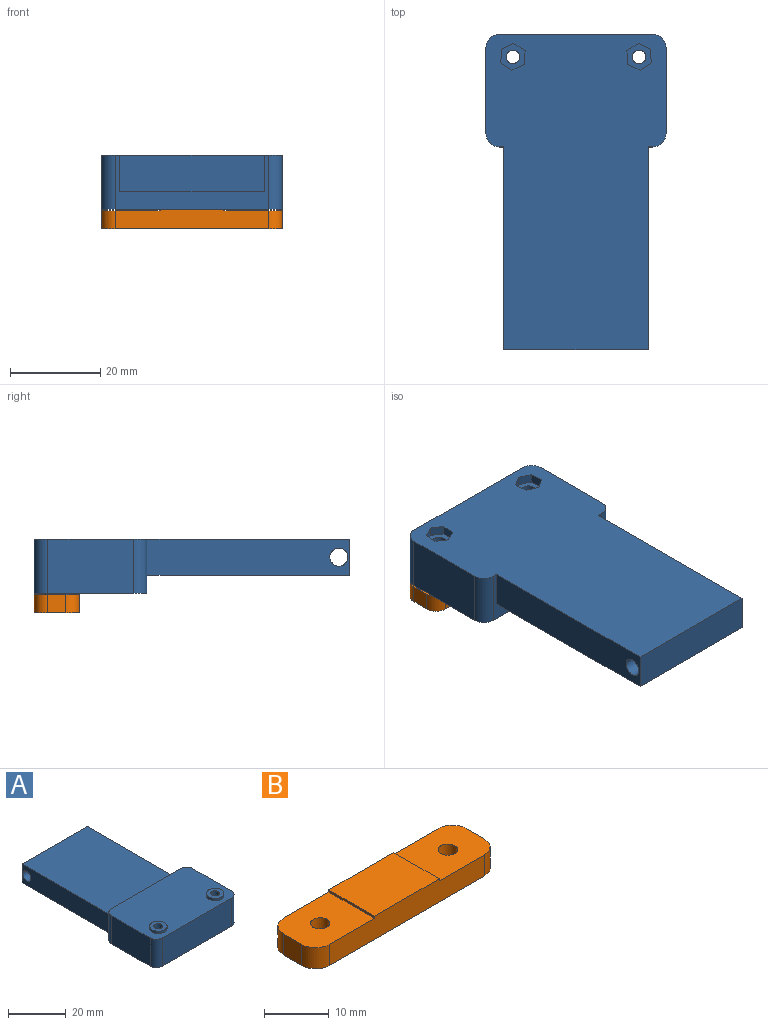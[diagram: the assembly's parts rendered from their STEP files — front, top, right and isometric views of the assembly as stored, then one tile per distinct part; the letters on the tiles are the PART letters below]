
ASSEMBLY  parts=2 mates=1
PART A: 35 faces, bbox 40x70x13 mm
  f0: plane 70x40mm, normal (0,0,-1), area 2385.4mm2, adj f2,f3,f4,f6,f8,f9,f10,f16
  f1: plane 40x25mm, normal (0,0,1), area 933.8mm2, adj f2,f3,f4,f6,f12,f14,f16,f17
  f2: plane 19x12mm, normal (-1,0,0), area 228mm2, adj f0,f1,f16,f18
  f3: plane 34x12mm, normal (0,-1,0), area 408mm2, adj f0,f1,f16,f17
  f4: plane 19x12mm, normal (1,0,0), area 228mm2, adj f0,f1,f17,f19
  f5: cylinder r=1.5mm len=11mm, axis (0,0,-1), area 103.7mm2, adj f15,f34
  f6: plane 34x12mm, normal (0,1,0), area 152mm2, adj f0,f1,f8,f9,f11,f18,f19
  f7: cylinder r=1.5mm len=11mm, axis (0,0,-1), area 103.7mm2, adj f13,f27
  f8: plane 45x8mm, normal (-1,0,0), area 347.4mm2, adj f0,f6,f10,f11,f20
  f9: plane 45x8mm, normal (1,0,0), area 347.4mm2, adj f0,f6,f10,f11,f20
  f10: plane 32x8mm, normal (0,1,0), area 256mm2, adj f0,f8,f9,f11
  f11: plane 45x32mm, normal (0,0,1), area 1440mm2, adj f6,f8,f9,f10
  f12: cylinder r=3.05mm len=6.1mm, axis (0,0,-1), area 19.2mm2, adj f1,f13
  f13: plane 6.1x6.1mm, normal (0,0,1), area 22.2mm2, adj f7,f12
  f14: cylinder r=3.05mm len=6.1mm, axis (0,0,-1), area 19.2mm2, adj f1,f15
  f15: plane 6.1x6.1mm, normal (0,0,1), area 22.2mm2, adj f5,f14
  f16: cylinder r=3mm len=12mm, axis (0,0,-1), area 56.5mm2, adj f0,f1,f2,f3
  f17: cylinder r=3mm len=12mm, axis (0,0,1), area 56.5mm2, adj f0,f1,f3,f4
  f18: cylinder r=3mm len=12mm, axis (0,0,1), area 56.5mm2, adj f0,f1,f2,f6
  f19: cylinder r=3mm len=12mm, axis (0,0,-1), area 56.5mm2, adj f0,f1,f4,f6
  f20: cylinder r=2mm len=32mm, axis (-1,0,0), area 402.1mm2, adj f8,f9
  f21: plane 2.99x2mm, normal (-1,-0.07,0), area 6mm2, adj f0,f22,f26,f27
  f22: plane 2.7x2mm, normal (-0.44,-0.9,0), area 6mm2, adj f0,f21,f23,f27
  f23: plane 2.49x2mm, normal (0.56,-0.83,0), area 6mm2, adj f0,f22,f24,f27
  f24: plane 2.99x2mm, normal (1,0.07,0), area 6mm2, adj f0,f23,f25,f27
  f25: plane 2.7x2mm, normal (0.44,0.9,0), area 6mm2, adj f0,f24,f26,f27
  f26: plane 2.49x2mm, normal (-0.56,0.83,0), area 6mm2, adj f0,f21,f25,f27
  f27: plane 5.99x5.4mm, normal (0,0,-1), area 16.3mm2, adj f7,f21,f22,f23,f24,f25,f26
  f28: plane 2.7x2mm, normal (0.44,-0.9,0), area 6mm2, adj f0,f29,f33,f34
  f29: plane 2.99x2mm, normal (1,-0.07,0), area 6mm2, adj f0,f28,f30,f34
  f30: plane 2.49x2mm, normal (0.56,0.83,0), area 6mm2, adj f0,f29,f31,f34
  f31: plane 2.7x2mm, normal (-0.44,0.9,0), area 6mm2, adj f0,f30,f32,f34
  f32: plane 2.99x2mm, normal (-1,0.07,0), area 6mm2, adj f0,f31,f33,f34
  f33: plane 2.49x2mm, normal (-0.56,-0.83,0), area 6mm2, adj f0,f28,f32,f34
  f34: plane 5.99x5.4mm, normal (0,0,-1), area 16.3mm2, adj f5,f28,f29,f30,f31,f32,f33
PART B: 16 faces, bbox 40x10x4.4 mm
  f0: plane 12.9x10mm, normal (0,0,1), area 118.1mm2, adj f2,f3,f4,f5,f10,f14,f15
  f1: plane 4x4mm, normal (-1,0,0), area 16mm2, adj f7,f8,f12,f13
  f2: plane 34x4.4mm, normal (0,-1,0), area 141.7mm2, adj f0,f7,f8,f9,f10,f11,f12,f14
  f3: plane 4x4mm, normal (1,0,0), area 16mm2, adj f0,f8,f14,f15
  f4: cylinder r=1.5mm len=4mm, axis (0,0,-1), area 37.7mm2, adj f0,f8
  f5: plane 34x4.4mm, normal (0,1,0), area 141.7mm2, adj f0,f7,f8,f9,f10,f11,f13,f15
  f6: cylinder r=1.5mm len=4mm, axis (0,0,-1), area 37.7mm2, adj f7,f8
  f7: plane 12.9x10mm, normal (0,0,1), area 118.1mm2, adj f1,f2,f5,f6,f9,f12,f13
  f8: plane 40x10mm, normal (0,0,-1), area 378.1mm2, adj f1,f2,f3,f4,f5,f6,f12,f13
  f9: plane 10x0.4mm, normal (-1,0,0), area 4mm2, adj f2,f5,f7,f11
  f10: plane 10x0.4mm, normal (1,0,0), area 4mm2, adj f0,f2,f5,f11
  f11: plane 14.2x10mm, normal (0,0,1), area 142mm2, adj f2,f5,f9,f10
  f12: cylinder r=3mm len=4mm, axis (0,0,-1), area 18.8mm2, adj f1,f2,f7,f8
  f13: cylinder r=3mm len=4mm, axis (0,0,1), area 18.8mm2, adj f1,f5,f7,f8
  f14: cylinder r=3mm len=4mm, axis (0,0,1), area 18.8mm2, adj f0,f2,f3,f8
  f15: cylinder r=3mm len=4mm, axis (0,0,-1), area 18.8mm2, adj f0,f3,f5,f8
PLACE A rot(axis=(1,0,0),180deg) t=(61.2,8.46,16.4)mm
PLACE B at identity
MATE fastened A.f7 <-> B.f6  axis (0,0,-1) through (55.08,4.23,4.4)mm
